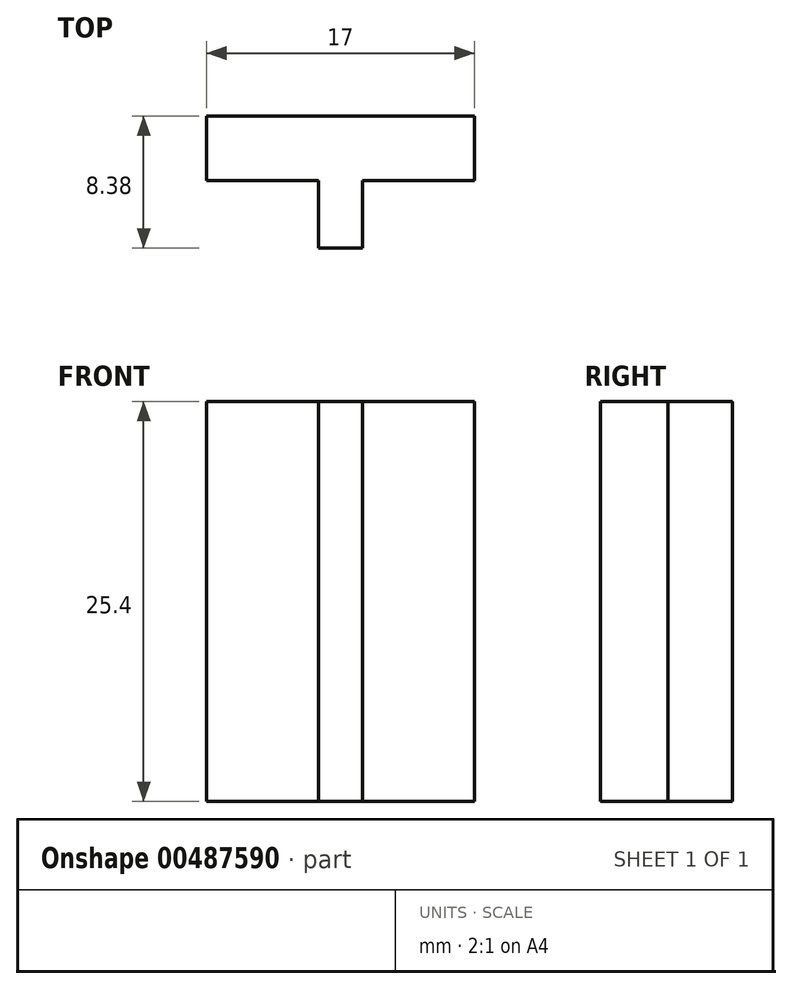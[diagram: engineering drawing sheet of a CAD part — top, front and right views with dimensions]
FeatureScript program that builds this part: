
annotation { "Feature Type Name" : "Feature", "Feature Type Description" : "" }
export const myFeature = defineFeature(function(context is Context, id is Id, definition is map)
    precondition{}
    {
        {
            var Q0;
            Q0=qCreatedBy(makeId("Top.planeOp"),FACE);
            var sketch = newSketch(context, id + "F0", { "sketchPlane" : qUnion([Q0])});
            skLineSegment(sketch, "E0", {"start": v(0, 0) * mm, "end": v(-8.5, 0) * mm});
            skLineSegment(sketch, "E1", {"start": v(-8.5, 0) * mm, "end": v(-8.5, -4.1) * mm});
            skLineSegment(sketch, "E2", {"start": v(-8.5, -4.1) * mm, "end": v(-1.4, -4.1) * mm});
            skLineSegment(sketch, "E3", {"start": v(-1.4, -4.1) * mm, "end": v(-1.4, -8.38) * mm});
            skLineSegment(sketch, "E4", {"start": v(-1.4, -8.38) * mm, "end": v(0, -8.38) * mm});
            skLineSegment(sketch, "E5.MirrorCS", {"start": v(0, 0) * mm, "end": v(8.5, 0) * mm});
            skLineSegment(sketch, "E6.MirrorCS", {"start": v(8.5, -4.1) * mm, "end": v(1.4, -4.1) * mm});
            skLineSegment(sketch, "E7.MirrorCS", {"start": v(1.4, -8.38) * mm, "end": v(0, -8.38) * mm});
            skLineSegment(sketch, "E8.MirrorCS", {"start": v(8.5, 0) * mm, "end": v(8.5, -4.1) * mm});
            skLineSegment(sketch, "E9.MirrorCS", {"start": v(1.4, -4.1) * mm, "end": v(1.4, -8.38) * mm});
            skSolve(sketch);
        }
        {
            var Q0;
            Q0=makeQuery(id+"F0.imprint","IMPRINT",FACE,{"disambiguationData":[TD([[makeQuery(id+"F0.imprint","IMPRINT",EDGE,{"derivedFrom":sQuery(id+"F0.wireOp",EDGE,"E0")}),1.0]])]});
            extrude(context, id + "F1", {"entities" : qUnion([Q0]), "depth" : 25.4 * mm});
        }
    });
